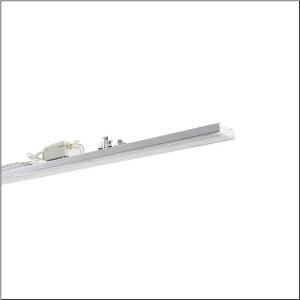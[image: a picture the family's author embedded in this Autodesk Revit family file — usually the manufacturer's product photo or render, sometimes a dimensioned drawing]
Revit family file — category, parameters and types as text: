
# Revit family: licross_r__21_recessed_mo_52tl12dn48xg_e767
name_source: partatom
category: Lighting Fixtures
units: mm (PartAtom-declared; Revit-internal decimal feet)

## family parameters
Cut with Voids When Loaded = No
Host = Face
Light Source = No
Part Type = Normal
Room Calculation Point = No
Round Connector Dimension = Use Diameter
Shared = No

## types (1)
- --- (1 x LED, 8000 lm, 44.2 W, 4000K)
    Apparent Load = 44 VA
    CIE Flux Codes = 72 92 99 100 100
    Color Rendering = 80
    Color Temperature = 4000K
    Default Elevation = 1800 mm
    Description = Licross® 21 Recessed MO, luminaire insert, of sheet steel, galvanised, coil coated, white, length: 1.500mm, width: 66mm, height: 67mm, LED rated luminous flux: 8.000lm, light colour: 840, control gear: DALI 2, with plug, 5-pole, with phase selection, mains connection: 220..240V, AC, 50/60Hz, rated input power: 44W, halogen-free wiring, primary optical cover: cover, of PMMA, light emission: direct distribution, primary light characteristic: symmetric, protection rating (complete): IP40, insulation class (complete): insulation class I (protective earthing), certification: CE, ENEC, VDE, UKCA, protection symbol: D if used in an environment without relevant dust loads with corresponding accessories, impact resistance: IK06, permissible ambient temperature for indoor applications: -25..+40°C, corresponds to IFS (International Featured Standards) requirements for safety and quality in the food industry, reducing of maximum allowable ambient temperature of 5°C with ceiling mounting, LABS conformity tested according to VDMA 24364:2018-05, packaging unit: 1 piece
    Height = 58 mm
    Lamp = 1 x LED
    Lamp Light Flux = 8000 lm
    Lamp Power = 44.2 W
    Lamp count = 1
    Length = 1500 mm
    Luminous efficacy = 181 lm/W
    Manufacturer = Siteco
    ModVariant = No
    Model = 52TL12DN48XG
    Mounting Place = Ceiling
    Mounting Type = Pendant
    Number of Poles = 1
    OnlyDefault = Yes
    Power Factor = 1
    Product Name = Licross® 21 Recessed MO
    Product group = luminaire insert
    ProductGroupID = 901
    Protection Class = Protection class I
    Protection Degree = IP 40
    RLX_Detail_Level = 1
    RLX_Emergency_Light_Flux = 0 lm
    RLX_Emergency_Type = 0
    RLX_Emergency_Type_DB = No
    RlxData = <blob elided: 24545 chars, md5=ce31287c>
    Socket = socket
    Standby Power = 0 W
    System Light Flux = 8000 lm
    System Power = 44 W
    Type Comments = factory setting: luminous flux: 100 % | dim-lin: 254 | 297 mA
    Type Image = l_1296930.jpg
    URL = http://relux.com
    VarID = @adj_057709
    Voltage = 0 V
    Weight = 0.00 kg
    Width = 66 mm

## geometry (parser evidence)
native form markers: Blend x4, Sweep x12
no freeform markers — native parametric forms only
